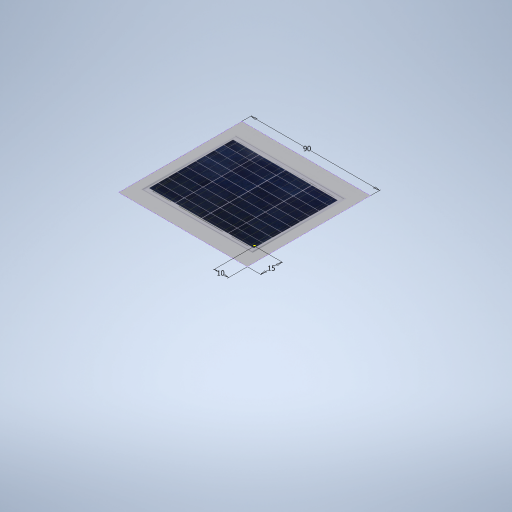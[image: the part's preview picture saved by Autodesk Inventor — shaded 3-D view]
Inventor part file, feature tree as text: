
AUTODESK INVENTOR PART (.ipt)
format: ipt  version: 2023 (Build 270158000, 158)  size: 384,512 bytes
history: native  units: mm
features: sketch x2, extrude x1, fillet x1, other x1
ambient origin geometry x8: Origin, YZ Plane, XZ Plane, XY Plane, X Axis, Y Axis, Z Axis, Center Point
bodies: Solid1 (feature_tree)
feature tree (5):
  extrude  "Extrusion1"  Depth=55.0mm
  fillet  "Fillet1"  Radius=3.0mm
  sketch  "Sketch2"  dims[d4=2.0mm d20=10.0mm d21=15.0mm d31=90.0mm d5=0.0mm d6=0.0mm d7=0.0mm]
  sketch  "Sketch1"  dims[d0=70.0mm d1=55.0mm d2=3.0mm d3=0.0mm]
  other  "Image1"
